# Revit family: Wall_Panel-Teknion-CWPH-Wall_Panel-R2021
name_source: partatom
category: Furniture
units: mm (PartAtom-declared; Revit-internal decimal feet)

## family parameters
Always vertical = Yes
Cut with Voids When Loaded = No
OmniClass Number = 23.40.20.00
OmniClass Title = General Furniture and Specialties
Room Calculation Point = No
Shared = Yes
Work Plane-Based = No

## types (5) — shared parameters
Assembly Code = E2020200
Manufacturer = Teknion
Manufacturer Fax = 416.661.4586
Part Number = CWPH
Product Documentation Link = https://www.teknion.com
Product Line = Chronicle
Product Page URL = https://www.teknion.com
Series = Chronicle
Sustainability Data = https://www.teknion.com
URL = www.teknion.com
Unit Weight URL = http://www.teknion.com
Warranty = http://www.teknion.com
zero-valued in all types: Default Elevation

## per-type parameters (varying)
| type | Description | Model |
| (1H) 1 High, 12.75" | Wall Panel, 1 High-12.75",Full Height | CWPH1HF__ |
| (2H) 2 High, 26.5" | Wall Panel, 2 High-26.5",Full Height | CWPH2HF__ |
| (3H) 3 High, 41.25" | Wall Panel, 3 High-41.25",Full Height | CWPH3HF__ |
| (4H) 4 High, 55" | Wall Panel, 4 High-55",Full Height | CWPH4HF |
| (3H) 3 High, Reduced Height by 1" | Wall Panel, 3 Hight-40.25",Reduced Height by 1" | CWPH3HR__ |

## geometry (parser evidence)
native form markers: Sweep x3
no freeform markers — native parametric forms only
